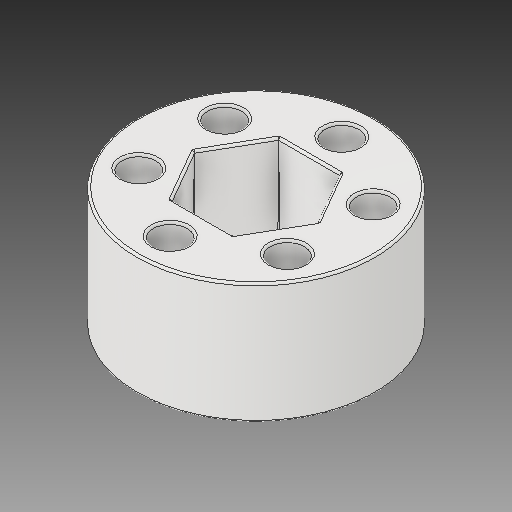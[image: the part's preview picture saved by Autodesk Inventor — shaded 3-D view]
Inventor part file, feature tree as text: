
AUTODESK INVENTOR PART (.ipt)
format: ipt  version: 2018 (Build 220112000, 112)  size: 235,008 bytes
history: native  units: in
note: dims shown in document units (in); Inventor stores cm internally (conversion verified against a paired STEP export)
features: fillet x1
ambient origin geometry x8: Origin, YZ Plane, XZ Plane, XY Plane, X Axis, Y Axis, Z Axis, Center Point
bodies: Solid1 (feature_tree)
feature tree (1):
  fillet  "Fillet2"  [1 undecoded]
note: 1 required parameter value undecoded (feature->parameter linkage not recoverable at this tier; creation-order binding heuristic only, values carry confidence <= 0.55)
